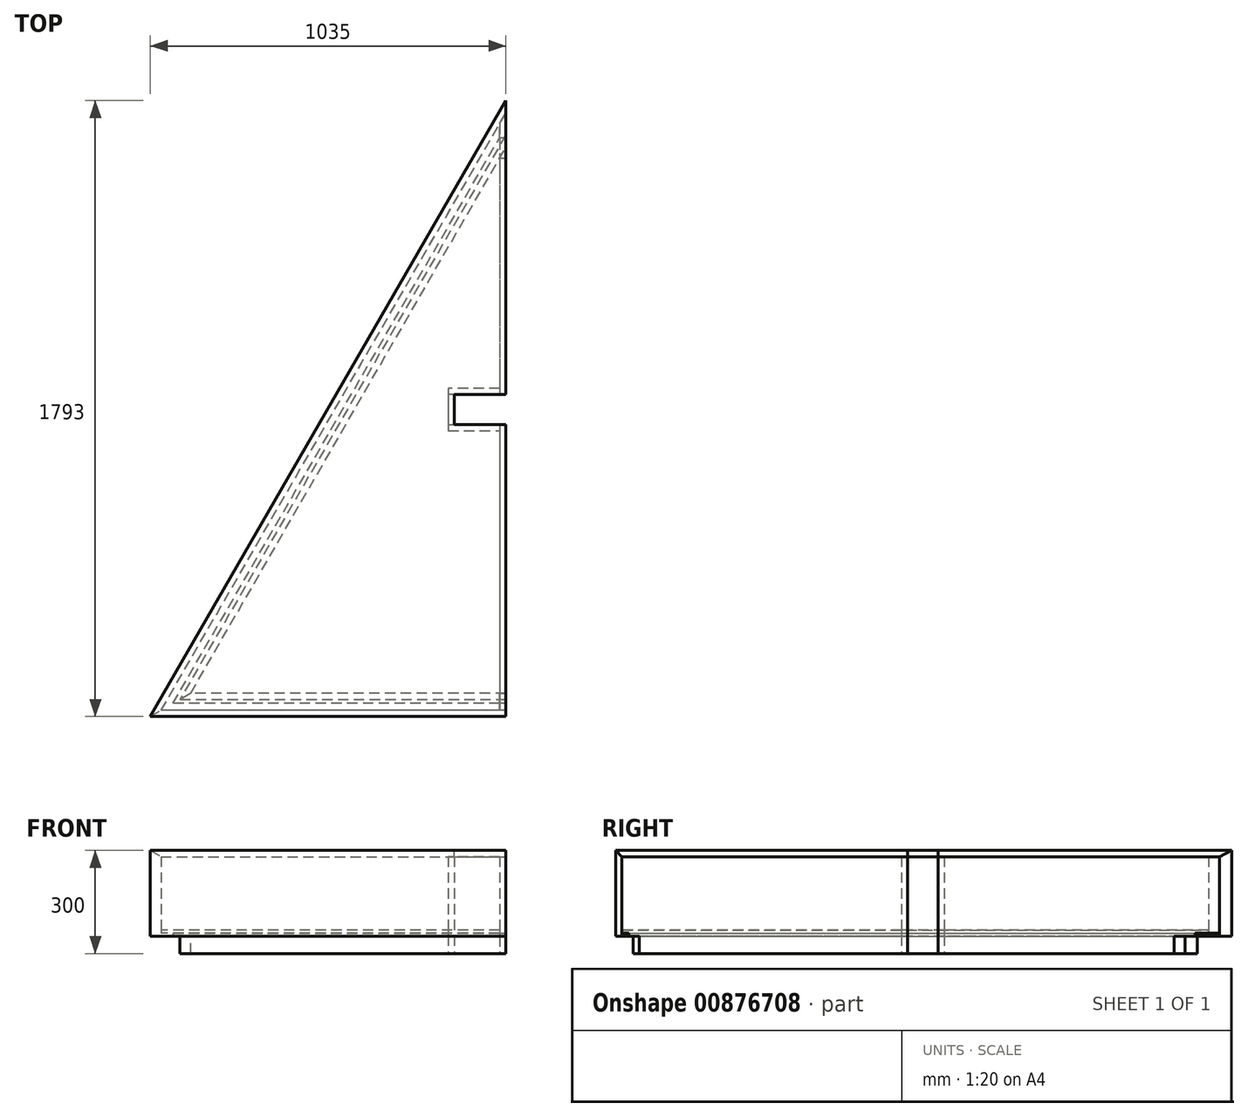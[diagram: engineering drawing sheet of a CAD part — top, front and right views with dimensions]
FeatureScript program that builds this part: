
annotation { "Feature Type Name" : "Feature", "Feature Type Description" : "" }
export const myFeature = defineFeature(function(context is Context, id is Id, definition is map)
    precondition{}
    {
        {
            var Q0;
            Q0=qCreatedBy(makeId("Top.planeOp"),FACE);
            var sketch = newSketch(context, id + "F0", { "sketchPlane" : qUnion([Q0])});
            skLineSegment(sketch, "E0", {"start": v(0, 0) * mm, "end": v(-1035, 0) * mm});
            skLineSegment(sketch, "E1", {"start": v(-1035, 0) * mm, "end": v(0, 1793) * mm});
            skLineSegment(sketch, "E2", {"start": v(0, 1793) * mm, "end": v(0, 938) * mm});
            skLineSegment(sketch, "E3", {"start": v(0, 938) * mm, "end": v(-168, 938) * mm});
            skLineSegment(sketch, "E4", {"start": v(-150, 938) * mm, "end": v(-150, 850) * mm});
            skLineSegment(sketch, "E5", {"start": v(-168, 850) * mm, "end": v(0, 850) * mm});
            skLineSegment(sketch, "E6", {"start": v(0, 850) * mm, "end": v(0, 0) * mm});
            skLineSegment(sketch, "E7.0", {"start": v(0, 18) * mm, "end": v(-1003.83, 18) * mm});
            skLineSegment(sketch, "E7.1", {"start": v(-18, 850) * mm, "end": v(-18, 18) * mm});
            skLineSegment(sketch, "E7.2", {"start": v(-18, 1725.81) * mm, "end": v(-18, 938) * mm});
            skLineSegment(sketch, "E7.3", {"start": v(-18, 956) * mm, "end": v(-168, 956) * mm});
            skLineSegment(sketch, "E7.4", {"start": v(-168, 956) * mm, "end": v(-168, 832) * mm});
            skLineSegment(sketch, "E7.5", {"start": v(-1003.83, 18) * mm, "end": v(-18, 1725.81) * mm});
            skLineSegment(sketch, "E7.6", {"start": v(-168, 832) * mm, "end": v(-18, 832) * mm});
            skLineSegment(sketch, "E8", {"start": v(-1035, 0) * mm, "end": v(-1003.83, 18) * mm});
            skLineSegment(sketch, "E9", {"start": v(-18, 1725.81) * mm, "end": v(0, 1757) * mm});
            skSolve(sketch);
        }
        {
            var Q0;
            {var subQ0=sQuery(id+"F0.wireOp",EDGE,"E1");Q0=makeQuery(id+"F0.imprint","IMPRINT",FACE,{"disambiguationData":[TD([[makeQuery(id+"F0.imprint","IMPRINT",EDGE,{"derivedFrom":subQ0}),-1.0]])]});}
            extrude(context, id + "F1", {"entities" : qUnion([Q0]), "depth" : 250 * mm, "offsetDistance" : 25 * mm});
        }
        {
            var Q0;
            {var subQ5=sQuery(id+"F0.wireOp",EDGE,"E0");Q0=makeQuery(id+"F0.imprint","IMPRINT",FACE,{"disambiguationData":[TD([[makeQuery(id+"F0.imprint","IMPRINT",EDGE,{"derivedFrom":subQ5}),-1.0]])]});}
            extrude(context, id + "F2", {"entities" : qUnion([Q0]), "depth" : 250 * mm, "offsetDistance" : 25 * mm});
        }
        {
            var Q0;
            {var subQ1=sQuery(id+"F0.wireOp",EDGE,"E6");var subQ5=sQuery(id+"F0.wireOp",EDGE,"E5");var subQ6=makeQuery(id+"F0.imprint","INTERSECT",VERTEX,{"derivedFrom":[subQ5,subQ1]});Q0=makeQuery(id+"F0.imprint","IMPRINT",FACE,{"disambiguationData":[TD([[makeQuery(id+"F0.imprint","IMPRINT",EDGE,{"disambiguationData":[TD([[subQ6,1.0]])],"derivedFrom":subQ5}),-1.0]])]});}
            var Q1;
            {var subQ0=sQuery(id+"F0.wireOp",EDGE,"E9");Q1=makeQuery(id+"F0.imprint","IMPRINT",FACE,{"disambiguationData":[TD([[makeQuery(id+"F0.imprint","IMPRINT",EDGE,{"derivedFrom":subQ0}),-1.0]])]});}
            var Q2;
            {var subQ3=sQuery(id+"F0.wireOp",EDGE,"E4");Q2=makeQuery(id+"F0.imprint","IMPRINT",FACE,{"disambiguationData":[TD([[makeQuery(id+"F0.imprint","IMPRINT",EDGE,{"derivedFrom":subQ3}),-1.0]])]});}
            extrude(context, id + "F3", {"entities" : qUnion([Q0, Q1, Q2]), "depth" : 232 * mm, "offsetDistance" : 25 * mm, "hasSecondDirection" : true, "secondDirectionOppositeDirection" : true, "secondDirectionDepth" : 50 * mm});
        }
        {
            var Q0;
            {var subQ0=sQuery(id+"F0.wireOp",EDGE,"E7.3");Q0=makeQuery(id+"F0.imprint","IMPRINT",FACE,{"disambiguationData":[TD([[makeQuery(id+"F0.imprint","IMPRINT",EDGE,{"derivedFrom":subQ0}),1.0]])]});}
            var Q1;
            {var subQ3=sQuery(id+"F0.wireOp",EDGE,"E7.6");Q1=makeQuery(id+"F0.imprint","IMPRINT",FACE,{"disambiguationData":[TD([[makeQuery(id+"F0.imprint","IMPRINT",EDGE,{"derivedFrom":subQ3}),1.0]])]});}
            extrude(context, id + "F4", {"entities" : qUnion([Q0, Q1]), "depth" : 232 * mm, "offsetDistance" : 25 * mm, "hasSecondDirection" : true, "secondDirectionOppositeDirection" : true, "secondDirectionDepth" : 50 * mm});
        }
        {
            var Q0;
            Q0=makeQuery(id+"F1.opExtrude","CAP_EDGE",EDGE,{"disambiguationData":[OSD([sQuery(id+"F0.wireOp",EDGE,"E7.5"),sQuery(id+"F0.wireOp",EDGE,"E9")])],"isStart":false});
            var Q1;
            Q1=makeQuery(id+"F2.opExtrude","CAP_EDGE",EDGE,{"disambiguationData":[OSD([sQuery(id+"F0.wireOp",EDGE,"E7.0")])],"isStart":false});
            chamfer(context, id + "F5", {"entities" : qUnion([Q0, Q1]), "width" : 18 * mm, "tangentPropagation" : true});
        }
        {
            var Q0;
            Q0=makeQuery(id+"F3.opExtrude","SWEPT_FACE",FACE,{"disambiguationData":[OSD([sQuery(id+"F0.wireOp",EDGE,"E6")])]});
            var sketch = newSketch(context, id + "F6", { "sketchPlane" : qUnion([Q0])});
            skLineSegment(sketch, "E10.bottom", {"start": v(0, 0) * mm, "end": v(68, 0) * mm});
            skLineSegment(sketch, "E10.top", {"start": v(0, -50) * mm, "end": v(68, -50) * mm});
            skLineSegment(sketch, "E10.left", {"start": v(0, 0) * mm, "end": v(0, -50) * mm});
            skLineSegment(sketch, "E10.right", {"start": v(68, 0) * mm, "end": v(68, -50) * mm});
            skSolve(sketch);
        }
        {
            var Q0;
            {var subQ0=sQuery(id+"F6.wireOp",EDGE,"E10.right");Q0=makeQuery(id+"F6.imprint","IMPRINT",FACE,{"disambiguationData":[TD([[makeQuery(id+"F6.imprint","IMPRINT",EDGE,{"derivedFrom":subQ0}),-1.0]])]});}
            extrude(context, id + "F7", {"entities" : qUnion([Q0]), "operationType" : NewBodyOperationType.REMOVE, "oppositeDirection" : true, "depth" : 25 * mm, "offsetDistance" : 25 * mm});
        }
        {
            var Q0;
            Q0=makeQuery(id+"F3.opExtrude","CAP_FACE",FACE,{"disambiguationData":[OSD([sQuery(id+"F0.wireOp",EDGE,"E2"),sQuery(id+"F0.wireOp",EDGE,"E3"),sQuery(id+"F0.wireOp",EDGE,"E7.2"),sQuery(id+"F0.wireOp",EDGE,"E9")])],"isStart":true});
            var sketch = newSketch(context, id + "F8", { "sketchPlane" : qUnion([Q0])});
            skLineSegment(sketch, "E11.1", {"start": v(-18, -1725.81) * mm, "end": v(0, -1757) * mm});
            skLineSegment(sketch, "E12.0", {"start": v(25.3, -1700.82) * mm, "end": v(43.3, -1732) * mm});
            skLineSegment(sketch, "E13", {"start": v(-18, -1725.81) * mm, "end": v(-18, -1625.8) * mm});
            skLineSegment(sketch, "E14", {"start": v(0, -1656.98) * mm, "end": v(25.3, -1700.82) * mm});
            skLineSegment(sketch, "E15", {"start": v(0, -1757) * mm, "end": v(43.3, -1732) * mm});
            skLineSegment(sketch, "E16", {"start": v(-18, -1625.8) * mm, "end": v(0, -1625.8) * mm});
            skLineSegment(sketch, "E17", {"start": v(0, -1625.8) * mm, "end": v(0, -1656.98) * mm});
            skLineSegment(sketch, "E18", {"start": v(-18, -1625.8) * mm, "end": v(0, -1656.98) * mm, "construction": true});
            skSolve(sketch);
        }
        {
            var Q0;
            {var subQ1=sQuery(id+"F8.wireOp",EDGE,"E11.1");Q0=makeQuery(id+"F8.imprint","IMPRINT",FACE,{"disambiguationData":[TD([[makeQuery(id+"F8.imprint","IMPRINT",EDGE,{"derivedFrom":subQ1}),1.0]])]});}
            extrude(context, id + "F9", {"entities" : qUnion([Q0]), "operationType" : NewBodyOperationType.REMOVE, "oppositeDirection" : true, "depth" : 50 * mm, "offsetDistance" : 25 * mm});
        }
        {
            var Q0;
            Q0=makeQuery(id+"F9.boolean.opBoolean","COPY",FACE,{"derivedFrom":makeQuery(id+"F9.opExtrude","CAP_FACE",FACE,{"disambiguationData":[OSD([sQuery(id+"F0.wireOp",EDGE,"E2"),sQuery(id+"F8.wireOp",EDGE,"E11.1"),sQuery(id+"F8.wireOp",EDGE,"E13"),sQuery(id+"F8.wireOp",EDGE,"E16"),sQuery(id+"F8.wireOp",EDGE,"E17")])],"isStart":false})});
            var sketch = newSketch(context, id + "F10", { "sketchPlane" : qUnion([Q0])});
            skLineSegment(sketch, "E19.0", {"start": v(-1003.83, -18) * mm, "end": v(-18, -1725.81) * mm});
            skLineSegment(sketch, "E20.0", {"start": v(-18, -18) * mm, "end": v(-1003.83, -18) * mm});
            skLineSegment(sketch, "E21.0", {"start": v(-18, -832) * mm, "end": v(-18, -68) * mm});
            skLineSegment(sketch, "E22.0", {"start": v(-168, -832) * mm, "end": v(-18, -832) * mm});
            skLineSegment(sketch, "E23.0", {"start": v(-18, -956) * mm, "end": v(-168, -956) * mm});
            skLineSegment(sketch, "E24.0", {"start": v(-18, -1725.81) * mm, "end": v(-18, -956) * mm});
            skPoint(sketch, "E25.orphan", {"position": v(0, -1757) * mm});
            skPoint(sketch, "E26.orphan", {"position": v(-18, -850) * mm});
            skPoint(sketch, "E27.orphan", {"position": v(-18, -938) * mm});
            skLineSegment(sketch, "E28", {"start": v(-168, -956) * mm, "end": v(-168, -832) * mm});
            skLineSegment(sketch, "E29", {"start": v(-18, -68) * mm, "end": v(-18, -18) * mm});
            skPoint(sketch, "E30.orphan", {"position": v(0, -18) * mm});
            skSolve(sketch);
        }
        {
            var Q0;
            {var subQ0=sQuery(id+"F10.wireOp",EDGE,"E19.0");Q0=makeQuery(id+"F10.imprint","IMPRINT",FACE,{"disambiguationData":[TD([[makeQuery(id+"F10.imprint","IMPRINT",EDGE,{"derivedFrom":subQ0}),1.0]])]});}
            extrude(context, id + "F11", {"entities" : qUnion([Q0]), "oppositeDirection" : true, "depth" : 18 * mm, "offsetDistance" : 25 * mm});
        }
        {
            var Q0;
            Q0=makeQuery(id+"F11.opExtrude","CAP_FACE",FACE,{"disambiguationData":[OSD([sQuery(id+"F10.wireOp",EDGE,"E19.0"),sQuery(id+"F10.wireOp",EDGE,"E20.0"),sQuery(id+"F10.wireOp",EDGE,"E21.0"),sQuery(id+"F10.wireOp",EDGE,"E22.0"),sQuery(id+"F10.wireOp",EDGE,"E23.0"),sQuery(id+"F10.wireOp",EDGE,"E24.0"),sQuery(id+"F10.wireOp",EDGE,"E28"),sQuery(id+"F10.wireOp",EDGE,"E29")])],"isStart":true});
            var sketch = newSketch(context, id + "F12", { "sketchPlane" : qUnion([Q0])});
            skLineSegment(sketch, "E31", {"start": v(0, -1692.99) * mm, "end": v(-948.4, -50) * mm});
            skLineSegment(sketch, "E32", {"start": v(-948.4, -50) * mm, "end": v(0, -50) * mm});
            skLineSegment(sketch, "E33", {"start": v(0, -50) * mm, "end": v(0, -68) * mm});
            skLineSegment(sketch, "E34", {"start": v(0, -68) * mm, "end": v(-917.23, -68) * mm});
            skLineSegment(sketch, "E35", {"start": v(-917.23, -68) * mm, "end": v(-948.4, -50) * mm});
            skLineSegment(sketch, "E36", {"start": v(-917.23, -68) * mm, "end": v(0, -1656.98) * mm});
            skLineSegment(sketch, "E37", {"start": v(0, -1656.98) * mm, "end": v(0, -1692.99) * mm});
            skSolve(sketch);
        }
        {
            var Q0;
            {var subQ0=sQuery(id+"F12.wireOp",EDGE,"E35");Q0=makeQuery(id+"F12.imprint","IMPRINT",FACE,{"disambiguationData":[TD([[makeQuery(id+"F12.imprint","IMPRINT",EDGE,{"derivedFrom":subQ0}),1.0]])]});}
            var Q1;
            {var subQ0=sQuery(id+"F12.wireOp",EDGE,"E37");Q1=makeQuery(id+"F12.imprint","IMPRINT",FACE,{"disambiguationData":[TD([[makeQuery(id+"F12.imprint","IMPRINT",EDGE,{"derivedFrom":subQ0}),-1.0]])]});}
            extrude(context, id + "F13", {"entities" : qUnion([Q0, Q1]), "depth" : 50 * mm, "offsetDistance" : 25 * mm});
        }
        {
            var Q0;
            {var subQ0=sQuery(id+"F12.wireOp",EDGE,"E35");Q0=makeQuery(id+"F12.imprint","IMPRINT",FACE,{"disambiguationData":[TD([[makeQuery(id+"F12.imprint","IMPRINT",EDGE,{"derivedFrom":subQ0}),-1.0]])]});}
            var Q1;
            {var subQ0=sQuery(id+"F12.wireOp",EDGE,"E33");Q1=makeQuery(id+"F12.imprint","IMPRINT",FACE,{"disambiguationData":[TD([[makeQuery(id+"F12.imprint","IMPRINT",EDGE,{"derivedFrom":subQ0}),-1.0]])]});}
            extrude(context, id + "F14", {"entities" : qUnion([Q0, Q1]), "depth" : 50 * mm, "offsetDistance" : 25 * mm});
        }
        {
            var Q0;
            Q0=qCreatedBy(makeId("Top.planeOp"),FACE);
            cPlane(context, id + "F15", {"entities" : qUnion([Q0]), "cplaneType" : CPlaneType.OFFSET, "offset" : 250 * mm, "width" : 150 * mm, "height" : 150 * mm});
        }
        {
            var Q0;
            Q0=qCreatedBy(id+"F15.planeOp",FACE);
            var sketch = newSketch(context, id + "F16", { "sketchPlane" : qUnion([Q0])});
            skLineSegment(sketch, "E38.0", {"start": v(0, 0) * mm, "end": v(-1035, 0) * mm});
            skLineSegment(sketch, "E39.0", {"start": v(-1035, 0) * mm, "end": v(0, 1793) * mm});
            skLineSegment(sketch, "E40", {"start": v(0, 0) * mm, "end": v(0, 850) * mm});
            skLineSegment(sketch, "E41.0", {"start": v(-150, 850) * mm, "end": v(0, 850) * mm});
            skLineSegment(sketch, "E42.0", {"start": v(-150, 938) * mm, "end": v(-150, 850) * mm});
            skLineSegment(sketch, "E43.0", {"start": v(0, 938) * mm, "end": v(-150, 938) * mm});
            skPoint(sketch, "E44.orphan", {"position": v(-18, 850) * mm});
            skPoint(sketch, "E45.orphan", {"position": v(-18, 938) * mm});
            skLineSegment(sketch, "E46.trimOffspring", {"start": v(0, 938) * mm, "end": v(0, 1793) * mm});
            skPoint(sketch, "E47.orphan", {"position": v(-168, 850) * mm});
            skPoint(sketch, "E48.orphan", {"position": v(-168, 938) * mm});
            skSolve(sketch);
        }
        {
            var Q0;
            Q0=makeQuery(id+"F16.imprint","IMPRINT",FACE,{"disambiguationData":[TD([[makeQuery(id+"F16.imprint","IMPRINT",EDGE,{"derivedFrom":sQuery(id+"F16.wireOp",EDGE,"E38.0")}),-1.0]])]});
            extrude(context, id + "F17", {"entities" : qUnion([Q0]), "oppositeDirection" : true, "depth" : 18 * mm, "offsetDistance" : 25 * mm});
        }
        {
            var Q0;
            Q0=makeQuery(id+"F17.opExtrude","CAP_EDGE",EDGE,{"disambiguationData":[OSD([sQuery(id+"F16.wireOp",EDGE,"E39.0")])],"isStart":false});
            var Q1;
            Q1=makeQuery(id+"F17.opExtrude","CAP_EDGE",EDGE,{"disambiguationData":[OSD([sQuery(id+"F16.wireOp",EDGE,"E38.0")])],"isStart":false});
            chamfer(context, id + "F18", {"entities" : qUnion([Q0, Q1]), "width" : 18 * mm, "tangentPropagation" : true});
        }
        {
            var Q0;
            {var subQ8=makeQuery(id+"F11.opExtrude","CAP_EDGE",EDGE,{"disambiguationData":[OSD([sQuery(id+"F10.wireOp",EDGE,"E19.0")])],"isStart":true});Q0=makeQuery(id+"F12.imprint","IMPRINT",FACE,{"disambiguationData":[TD([[makeQuery(id+"F12.imprint","IMPRINT",EDGE,{"derivedFrom":subQ8}),1.0]])]});}
            var sketch = newSketch(context, id + "F19", { "sketchPlane" : qUnion([Q0])});
            skLineSegment(sketch, "E49.0", {"start": v(0, -18) * mm, "end": v(-1003.83, -18) * mm});
            skLineSegment(sketch, "E50.0", {"start": v(-1003.83, -18) * mm, "end": v(0, -1757) * mm});
            skLineSegment(sketch, "E51.0", {"start": v(-969.19, -38) * mm, "end": v(-18, -1685.8) * mm});
            skLineSegment(sketch, "E51.1", {"start": v(0, -38) * mm, "end": v(-969.19, -38) * mm});
            skLineSegment(sketch, "E52", {"start": v(0, -18) * mm, "end": v(0, -38) * mm});
            skLineSegment(sketch, "E53", {"start": v(0, -1757) * mm, "end": v(0, -1685.8) * mm});
            skLineSegment(sketch, "E54", {"start": v(-18, -1685.8) * mm, "end": v(0, -1685.8) * mm});
            skSolve(sketch);
        }
        {
            var Q0;
            Q0 = qSketchRegion(id + "F19", true);
            extrude(context, id + "F20", {"entities" : qUnion([Q0]), "operationType" : NewBodyOperationType.REMOVE, "oppositeDirection" : true, "depth" : 9 * mm, "offsetDistance" : 25 * mm});
        }
    });
